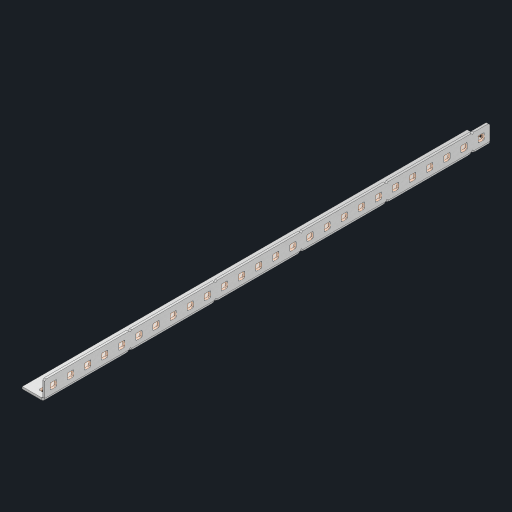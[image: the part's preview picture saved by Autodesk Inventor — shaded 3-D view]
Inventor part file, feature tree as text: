
AUTODESK INVENTOR PART (.ipt)
format: ipt  version: 2023 (Build 270158000, 158)  size: 889,344 bytes
history: native  units: in
note: dims shown in document units (in); Inventor stores cm internally (conversion verified against a paired STEP export)
features: other x57, extrude x51, sheet_metal_op x10, sketch x8, mirror x1, pattern_linear x1, chamfer x1
ambient origin geometry x8: Origin, YZ Plane, XZ Plane, XY Plane, X Axis, Y Axis, Z Axis, Center Point
bodies: Solid1 (feature_tree), Body (feature_tree)
feature tree (129):
  other  "Flange Pattern Plane"
  sheet_metal_op  "Flange Pattern"
  sheet_metal_op  "Body Pattern"
  other  "Arc Length"
  mirror  "Notch Mirror"
  pattern_linear  "Notch Pattern"  Spacing1=0.25in  [1 undecoded]
  chamfer  "End Chamfer"
  extrude  "Half Cut"  Depth=0.0625in
  sketch  "Sketch1"  dims[d0=1.5in]
  other  "Plate1"
  sketch  "Sketch2"  dims[d1=13.0in]
  other  "Plate2"
  sheet_metal_op  "Bend1"
  sheet_metal_op  "Corner1"
  sketch  "Sketch3"  dims[d2=0.0625in]
  other  "Flange Pattern Sketch"
  sketch  "Sketch7"  dims[d3=0.0625in]
  other  "Srf1"
  other  "Srf2"
  sketch  "Sketch8"  dims[d4=0.0312in]
  sketch  "Sketch9"  dims[d5=0.125in]
  other  "Srf91"
  sheet_metal_op  "Body Pattern Sketch"
  other  "Srf92"
  sketch  "Sketch13"  dims[d6=0.0625in]
  sketch  "Sketch14"  dims[d7=0.5in d8=90.0deg d9=0.0312in d10=0.25in d11=0.0625in d12=0.0625in d16=0.182in d17=0.02in d18=0.0625in d19=0.0in d20=0.25in d21=0.25in d46=0.172in d47=1.0in d48=0.0in d49=0.182in d50=0.02in d51=0.25in d52=0.25in d53=0.0625in d54=0.0in d55=0.172in d56=1.0in d57=0.0in d60=10.2362in d62=0.5in d63=0.3937in d65=0.5in d85=0.1473in d86=0.1782in d88=0.04in d89=0.0625in d90=0.0in d91=0.04in d92=0.0491in d95=2.5in d96=0.04in d97=0.25in d98=45.0deg d101=0.0in d102=2.497in d131=0.5in d132=10.2362in d134=0.5in d139=0.5in]
  other  "Srf856"
  other  "Srf1310"
  other  "Srf1311"
  other  "Srf1312"
  other  "Srf1376"
  other  "Srf1377"
  other  "Srf1728"
  other  "Srf1755"
  other  "Srf1878"
  other  "Srf1879"
  other  "Srf1880"
  other  "Srf1881"
  other  "Srf1882"
  other  "Srf1883"
  other  "Srf1884"
  other  "Srf1885"
  other  "Srf1886"
  other  "Srf1887"
  other  "Srf1888"
  other  "Srf1889"
  other  "Srf1890"
  other  "Srf1891"
  other  "Srf1892"
  other  "Srf1893"
  other  "Srf1894"
  other  "Srf1895"
  other  "Srf1896"
  other  "Srf1897"
  other  "Srf1942"
  other  "Srf1943"
  other  "Srf1944"
  other  "Srf1945"
  other  "Srf1946"
  other  "Srf1947"
  other  "Srf1948"
  other  "Srf1949"
  other  "Srf1950"
  other  "Srf1951"
  other  "Srf1952"
  other  "Srf1953"
  other  "Srf1954"
  other  "Srf1955"
  other  "Srf1956"
  other  "Srf1957"
  other  "Srf1958"
  other  "Srf1959"
  other  "Srf1960"
  other  "Srf1961"
  sheet_metal_op  "Flange Stamp"
  sheet_metal_op  "Flange Circle"
  sheet_metal_op  "Body Stamp"
  sheet_metal_op  "Body Circle"
  sheet_metal_op  "Notch"
  extrude  "ExtrusionSrf2"  Depth=0.0625in
  extrude  "ExtrusionSrf92"  Depth=0.5in
  extrude  "ExtrusionSrf856"  Depth=0.02in
  extrude  "ExtrusionSrf1310"  Depth=0.0625in
  extrude  "ExtrusionSrf1311"  TaperAngle=0.0deg  [1 undecoded]
  extrude  "ExtrusionSrf1312"  Depth=0.5in
  extrude  "ExtrusionSrf1376"  Depth=0.5in
  extrude  "ExtrusionSrf1377"  Depth=0.5in
  extrude  "ExtrusionSrf1728"  Depth=0.5in TaperAngle=0.0deg
  extrude  "ExtrusionSrf1755"  Depth=0.5in
  extrude  "ExtrusionSrf1878"  Depth=0.02in
  extrude  "ExtrusionSrf1879"  Depth=0.5in
  extrude  "ExtrusionSrf1880"  Depth=0.5in
  extrude  "ExtrusionSrf1881"  Depth=0.0625in
  extrude  "ExtrusionSrf1882"  TaperAngle=0.0deg  [1 undecoded]
  extrude  "ExtrusionSrf1883"  Depth=0.5in
  extrude  "ExtrusionSrf1884"  Depth=0.5in TaperAngle=0.0deg
  extrude  "ExtrusionSrf1885"  Depth=0.5in
  extrude  "ExtrusionSrf1886"  Depth=0.5in
  extrude  "ExtrusionSrf1887"  Depth=0.5in
  extrude  "ExtrusionSrf1888"  Depth=0.5in
  extrude  "ExtrusionSrf1889"  Depth=0.5in
  extrude  "ExtrusionSrf1890"  Depth=0.0625in
  extrude  "ExtrusionSrf1891"  TaperAngle=0.0deg  [1 undecoded]
  extrude  "ExtrusionSrf1892"  Depth=0.5in
  extrude  "ExtrusionSrf1893"  Depth=0.5in
  extrude  "ExtrusionSrf1894"  Depth=0.5in
  extrude  "ExtrusionSrf1895"  Depth=0.5in TaperAngle=45.0deg
  extrude  "ExtrusionSrf1896"  TaperAngle=0.0deg  [1 undecoded]
  extrude  "ExtrusionSrf1897"  Depth=0.5in
  extrude  "ExtrusionSrf1942"  Depth=0.5in
  extrude  "ExtrusionSrf1943"  Depth=0.5in
  extrude  "ExtrusionSrf1944"  Depth=0.5in
  extrude  "ExtrusionSrf1945"  Depth=0.5in
  extrude  "ExtrusionSrf1946"  [1 undecoded]
  extrude  "ExtrusionSrf1947"  [1 undecoded]
  extrude  "ExtrusionSrf1948"  [1 undecoded]
  extrude  "ExtrusionSrf1949"  [1 undecoded]
  extrude  "ExtrusionSrf1950"  [1 undecoded]
  extrude  "ExtrusionSrf1951"  [1 undecoded]
  extrude  "ExtrusionSrf1952"  [1 undecoded]
  extrude  "ExtrusionSrf1953"  [1 undecoded]
  extrude  "ExtrusionSrf1954"  [1 undecoded]
  extrude  "ExtrusionSrf1955"  [1 undecoded]
  extrude  "ExtrusionSrf1956"  [1 undecoded]
  extrude  "ExtrusionSrf1957"  [1 undecoded]
  extrude  "ExtrusionSrf1958"  [1 undecoded]
  extrude  "ExtrusionSrf1959"  [1 undecoded]
  extrude  "ExtrusionSrf1960"  [1 undecoded]
  extrude  "ExtrusionSrf1961"  [1 undecoded]
note: 21 required parameter values undecoded (feature->parameter linkage not recoverable at this tier; creation-order binding heuristic only, values carry confidence <= 0.55)
